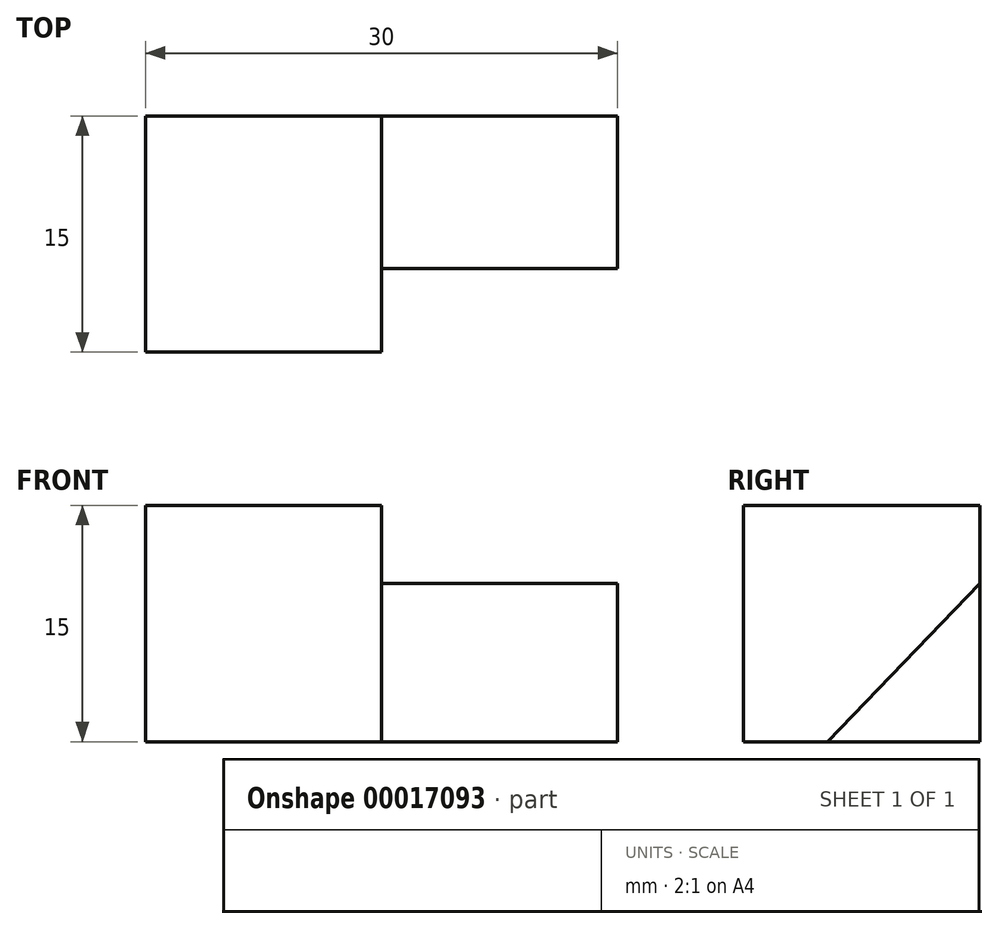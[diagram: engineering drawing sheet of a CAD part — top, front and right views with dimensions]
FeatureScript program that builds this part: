
annotation { "Feature Type Name" : "Feature", "Feature Type Description" : "" }
export const myFeature = defineFeature(function(context is Context, id is Id, definition is map)
    precondition{}
    {
        {
            var Q0;
            Q0=qCreatedBy(makeId("Right.planeOp"),FACE);
            var sketch = newSketch(context, id + "F0", { "sketchPlane" : qUnion([Q0])});
            skLineSegment(sketch, "E0.bottom", {"start": v(-4.9, 5.05) * mm, "end": v(10.1, 5.05) * mm});
            skLineSegment(sketch, "E0.top", {"start": v(-4.9, -9.95) * mm, "end": v(10.1, -9.95) * mm});
            skLineSegment(sketch, "E0.left", {"start": v(-4.9, 5.05) * mm, "end": v(-4.9, -9.95) * mm});
            skLineSegment(sketch, "E0.right", {"start": v(10.1, 5.05) * mm, "end": v(10.1, -9.95) * mm});
            skSolve(sketch);
        }
        {
            var Q0;
            Q0=makeQuery(id+"F0.imprint","IMPRINT",FACE,{"disambiguationData":[TD([[makeQuery(id+"F0.imprint","IMPRINT",EDGE,{"derivedFrom":sQuery(id+"F0.wireOp",EDGE,"E0.bottom")}),-1.0]])]});
            extrude(context, id + "F1", {"entities" : qUnion([Q0]), "depth" : 15 * mm});
        }
        {
            var Q0;
            Q0=makeQuery(id+"F1.opExtrude","CAP_FACE",FACE,{"disambiguationData":[OSD([sQuery(id+"F0.wireOp",EDGE,"E0.bottom"),sQuery(id+"F0.wireOp",EDGE,"E0.top"),sQuery(id+"F0.wireOp",EDGE,"E0.left"),sQuery(id+"F0.wireOp",EDGE,"E0.right")])],"isStart":false});
            var sketch = newSketch(context, id + "F2", { "sketchPlane" : qUnion([Q0])});
            skLineSegment(sketch, "E1", {"start": v(10.1, 0.1) * mm, "end": v(0.42, -9.95) * mm});
            skSolve(sketch);
        }
        {
            var Q0;
            {var subQ1=sQuery(id+"F2.wireOp",EDGE,"E1");Q0=makeQuery(id+"F2.imprint","IMPRINT",FACE,{"disambiguationData":[TD([[makeQuery(id+"F2.imprint","IMPRINT",EDGE,{"derivedFrom":subQ1}),1.0]])]});}
            extrude(context, id + "F3", {"entities" : qUnion([Q0]), "operationType" : NewBodyOperationType.ADD, "depth" : 15 * mm});
        }
    });
